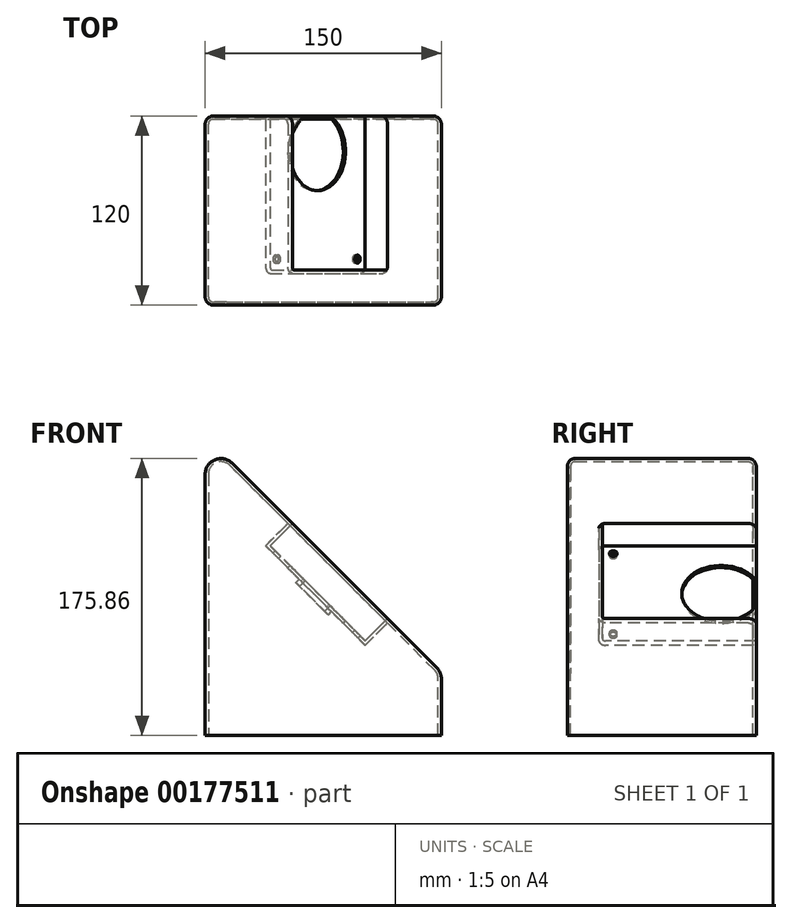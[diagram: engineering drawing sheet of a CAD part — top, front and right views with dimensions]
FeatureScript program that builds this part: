
annotation { "Feature Type Name" : "Feature", "Feature Type Description" : "" }
export const myFeature = defineFeature(function(context is Context, id is Id, definition is map)
    precondition{}
    {
        {
            var Q0;
            Q0=qCreatedBy(makeId("Front.planeOp"),FACE);
            var sketch = newSketch(context, id + "F0", { "sketchPlane" : qUnion([Q0])});
            skLineSegment(sketch, "E0", {"start": v(-84.02, -102.86) * mm, "end": v(65.98, -102.86) * mm});
            skLineSegment(sketch, "E1", {"start": v(65.98, -102.86) * mm, "end": v(65.98, -67) * mm});
            skLineSegment(sketch, "E2", {"start": v(63.05, -59.93) * mm, "end": v(-66.95, 70.07) * mm});
            skLineSegment(sketch, "E3", {"start": v(-84.02, 63) * mm, "end": v(-84.02, -102.86) * mm});
            skPoint(sketch, "E4.visualSharp", {"position": v(-84.02, 87.14) * mm});
            skArc(sketch, "E4.filletArc", {"start": v(-66.95, 70.07) * mm, "mid": v(-77.84, 72.24) * mm, "end": v(-84.02, 63) * mm});
            skPoint(sketch, "E5.visualSharp", {"position": v(65.98, -62.86) * mm});
            skArc(sketch, "E5.filletArc", {"start": v(65.98, -67) * mm, "mid": v(65.22, -63.17) * mm, "end": v(63.05, -59.93) * mm});
            skSolve(sketch);
        }
        {
            var Q0;
            Q0=makeQuery(id+"F0.imprint","IMPRINT",FACE,{"disambiguationData":[TD([[makeQuery(id+"F0.imprint","IMPRINT",EDGE,{"derivedFrom":sQuery(id+"F0.wireOp",EDGE,"E0")}),1.0]])]});
            extrude(context, id + "F1", {"entities" : qUnion([Q0]), "depth" : 120 * mm, "symmetric" : true});
        }
        {
            var Q0;
            Q0=makeQuery(id+"F1.opExtrude","SWEPT_FACE",FACE,{"disambiguationData":[OSD([sQuery(id+"F0.wireOp",EDGE,"E2")])]});
            var sketch = newSketch(context, id + "F2", { "sketchPlane" : qUnion([Q0])});
            skLineSegment(sketch, "E6.bottom", {"start": v(67.66, 42.7) * mm, "end": v(-35.84, 42.7) * mm});
            skLineSegment(sketch, "E6.top", {"start": v(67.66, -42.7) * mm, "end": v(-35.84, -42.7) * mm});
            skLineSegment(sketch, "E6.left", {"start": v(69.66, 40.7) * mm, "end": v(69.66, -40.7) * mm});
            skLineSegment(sketch, "E6.right", {"start": v(-37.84, 40.7) * mm, "end": v(-37.84, -40.7) * mm});
            skPoint(sketch, "E6.middle", {"position": v(15.91, 0) * mm});
            skPoint(sketch, "E7.visualSharp", {"position": v(-37.84, -42.7) * mm});
            skArc(sketch, "E7.filletArc", {"start": v(-37.84, -40.7) * mm, "mid": v(-37.25, -42.11) * mm, "end": v(-35.84, -42.7) * mm});
            skPoint(sketch, "E8.visualSharp", {"position": v(-37.84, 42.7) * mm});
            skArc(sketch, "E8.filletArc", {"start": v(-35.84, 42.7) * mm, "mid": v(-37.25, 42.11) * mm, "end": v(-37.84, 40.7) * mm});
            skPoint(sketch, "E9.visualSharp", {"position": v(69.66, 42.7) * mm});
            skArc(sketch, "E9.filletArc", {"start": v(69.66, 40.7) * mm, "mid": v(69.08, 42.11) * mm, "end": v(67.66, 42.7) * mm});
            skPoint(sketch, "E10.visualSharp", {"position": v(69.66, -42.7) * mm});
            skArc(sketch, "E10.filletArc", {"start": v(67.66, -42.7) * mm, "mid": v(69.08, -42.11) * mm, "end": v(69.66, -40.7) * mm});
            skCircle(sketch, "E11", {"center": v(37.66, 0) * mm, "radius": 25 * mm});
            skCircle(sketch, "E12", {"center": v(-30.84, -35.7) * mm, "radius": 2.5 * mm});
            skCircle(sketch, "E13", {"center": v(-30.84, 35.7) * mm, "radius": 2.5 * mm});
            skCircle(sketch, "E14", {"center": v(62.66, 35.7) * mm, "radius": 2.5 * mm});
            skCircle(sketch, "E15", {"center": v(62.66, -35.7) * mm, "radius": 2.5 * mm});
            skSolve(sketch);
        }
        {
            var Q0;
            Q0=makeQuery(id+"F2.imprint","IMPRINT",FACE,{"disambiguationData":[TD([[makeQuery(id+"F2.imprint","IMPRINT",EDGE,{"derivedFrom":sQuery(id+"F2.wireOp",EDGE,"E6.bottom")}),1.0]])]});
            var Q1;
            Q1=makeQuery(id+"F2.imprint","IMPRINT",FACE,{"disambiguationData":[TD([[makeQuery(id+"F2.imprint","IMPRINT",EDGE,{"derivedFrom":sQuery(id+"F2.wireOp",EDGE,"E11")}),1.0]])]});
            var Q2;
            Q2=makeQuery(id+"F2.imprint","IMPRINT",FACE,{"disambiguationData":[TD([[makeQuery(id+"F2.imprint","IMPRINT",EDGE,{"derivedFrom":sQuery(id+"F2.wireOp",EDGE,"E13")}),1.0]])]});
            var Q3;
            Q3=makeQuery(id+"F2.imprint","IMPRINT",FACE,{"disambiguationData":[TD([[makeQuery(id+"F2.imprint","IMPRINT",EDGE,{"derivedFrom":sQuery(id+"F2.wireOp",EDGE,"E14")}),1.0]])]});
            var Q4;
            Q4=makeQuery(id+"F2.imprint","IMPRINT",FACE,{"disambiguationData":[TD([[makeQuery(id+"F2.imprint","IMPRINT",EDGE,{"derivedFrom":sQuery(id+"F2.wireOp",EDGE,"E15")}),1.0]])]});
            var Q5;
            Q5=makeQuery(id+"F2.imprint","IMPRINT",FACE,{"disambiguationData":[TD([[makeQuery(id+"F2.imprint","IMPRINT",EDGE,{"derivedFrom":sQuery(id+"F2.wireOp",EDGE,"E12")}),1.0]])]});
            extrude(context, id + "F3", {"entities" : qUnion([Q0, Q1, Q2, Q3, Q4, Q5]), "operationType" : NewBodyOperationType.REMOVE, "oppositeDirection" : true, "depth" : 20 * mm});
        }
        {
            var Q0;
            Q0=makeQuery(id+"F1.opExtrude","CAP_EDGE",EDGE,{"disambiguationData":[OSD([sQuery(id+"F0.wireOp",EDGE,"E2")])],"isStart":true});
            var Q1;
            Q1=makeQuery(id+"F1.opExtrude","CAP_EDGE",EDGE,{"disambiguationData":[OSD([sQuery(id+"F0.wireOp",EDGE,"E2")])],"isStart":false});
            fillet(context, id + "F4", {"entities" : qUnion([Q0, Q1]), "radius" : 5 * mm, "tangentPropagation" : true, "allowEdgeOverflow" : false});
        }
        {
            var Q0;
            Q0=makeQuery(id+"F1.opExtrude","SWEPT_FACE",FACE,{"disambiguationData":[OSD([sQuery(id+"F0.wireOp",EDGE,"E0")])]});
            shell(context, id + "F5", {"entities" : qUnion([Q0]), "thickness" : 2 * mm});
        }
        {
            var Q0;
            Q0=makeQuery(id+"F2.imprint","IMPRINT",FACE,{"disambiguationData":[TD([[makeQuery(id+"F2.imprint","IMPRINT",EDGE,{"derivedFrom":sQuery(id+"F2.wireOp",EDGE,"E11")}),1.0]])]});
            var Q1;
            Q1=makeQuery(id+"F2.imprint","IMPRINT",FACE,{"disambiguationData":[TD([[makeQuery(id+"F2.imprint","IMPRINT",EDGE,{"derivedFrom":sQuery(id+"F2.wireOp",EDGE,"E13")}),1.0]])]});
            var Q2;
            Q2=makeQuery(id+"F2.imprint","IMPRINT",FACE,{"disambiguationData":[TD([[makeQuery(id+"F2.imprint","IMPRINT",EDGE,{"derivedFrom":sQuery(id+"F2.wireOp",EDGE,"E12")}),1.0]])]});
            var Q3;
            Q3=makeQuery(id+"F2.imprint","IMPRINT",FACE,{"disambiguationData":[TD([[makeQuery(id+"F2.imprint","IMPRINT",EDGE,{"derivedFrom":sQuery(id+"F2.wireOp",EDGE,"E14")}),1.0]])]});
            var Q4;
            Q4=makeQuery(id+"F2.imprint","IMPRINT",FACE,{"disambiguationData":[TD([[makeQuery(id+"F2.imprint","IMPRINT",EDGE,{"derivedFrom":sQuery(id+"F2.wireOp",EDGE,"E15")}),1.0]])]});
            extrude(context, id + "F6", {"entities" : qUnion([Q0, Q1, Q2, Q3, Q4]), "operationType" : NewBodyOperationType.REMOVE, "oppositeDirection" : true, "depth" : 25 * mm});
        }
    });
